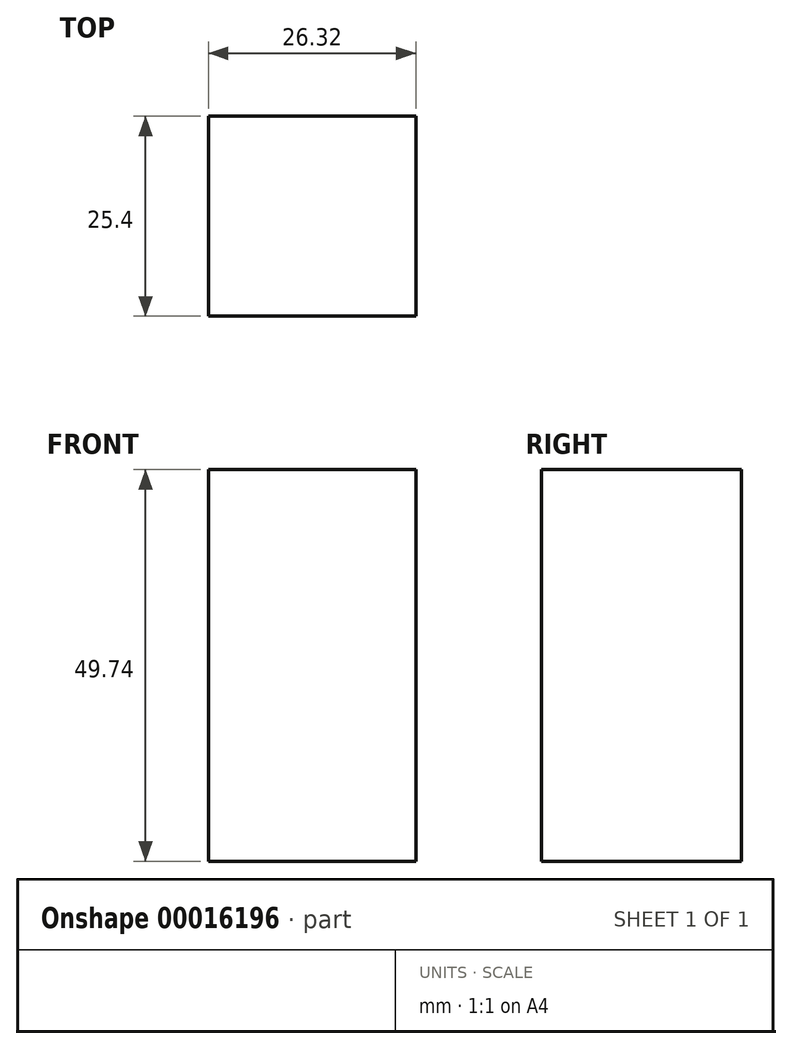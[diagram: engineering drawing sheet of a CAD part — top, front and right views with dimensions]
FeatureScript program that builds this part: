
annotation { "Feature Type Name" : "Feature", "Feature Type Description" : "" }
export const myFeature = defineFeature(function(context is Context, id is Id, definition is map)
    precondition{}
    {
        {
            var Q0;
            Q0=qCreatedBy(makeId("Front.planeOp"),FACE);
            var sketch = newSketch(context, id + "F0", { "sketchPlane" : qUnion([Q0])});
            skLineSegment(sketch, "E0.bottom", {"start": v(-76.37, 63.02) * mm, "end": v(-50.05, 63.02) * mm});
            skLineSegment(sketch, "E0.top", {"start": v(-76.37, 13.28) * mm, "end": v(-50.05, 13.28) * mm});
            skLineSegment(sketch, "E0.left", {"start": v(-76.37, 63.02) * mm, "end": v(-76.37, 13.28) * mm});
            skLineSegment(sketch, "E0.right", {"start": v(-50.05, 63.02) * mm, "end": v(-50.05, 13.28) * mm});
            skSolve(sketch);
        }
        {
            var Q0;
            Q0=makeQuery(id+"F0.imprint","IMPRINT",FACE,{"disambiguationData":[TD([[makeQuery(id+"F0.imprint","IMPRINT",EDGE,{"derivedFrom":sQuery(id+"F0.wireOp",EDGE,"E0.bottom")}),-1.0]])]});
            extrude(context, id + "F1", {"entities" : qUnion([Q0]), "depth" : 25.4 * mm});
        }
    });
